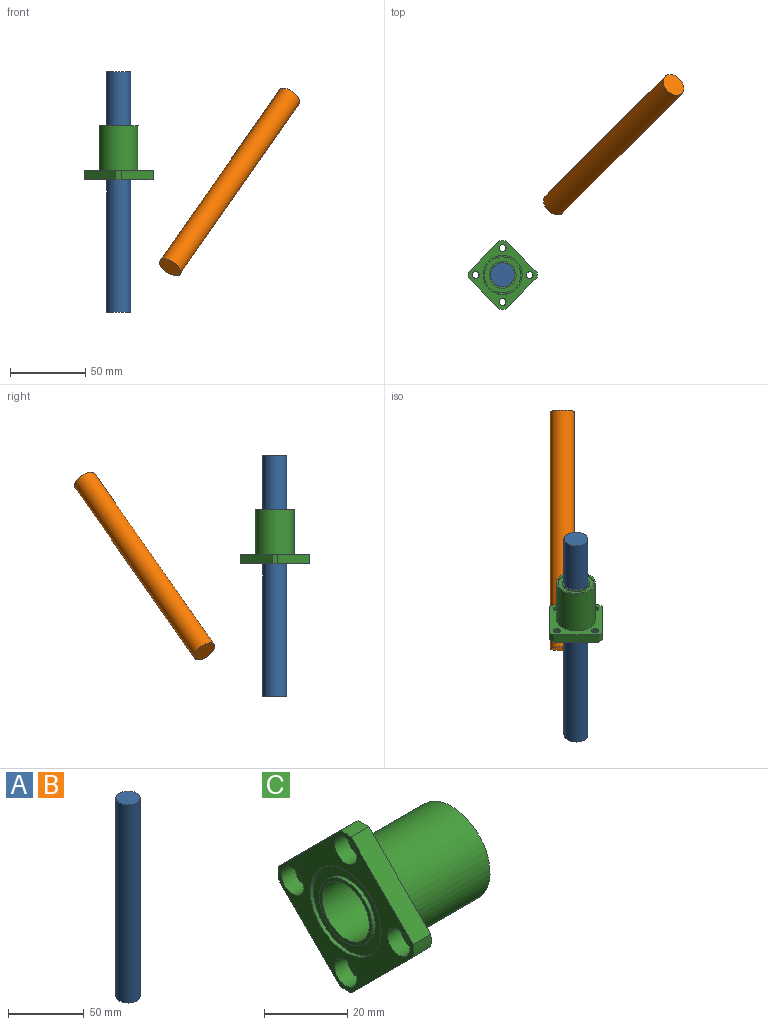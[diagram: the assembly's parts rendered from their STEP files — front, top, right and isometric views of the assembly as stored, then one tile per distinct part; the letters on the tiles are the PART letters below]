
ASSEMBLY  parts=3 mates=1
PART A: 3 faces, bbox 16x16x160 mm
  f0: cylinder r=8mm len=160mm, axis (0,0,1), area 8042.5mm2, adj f1,f2
  f1: plane 16x16mm, normal (0,0,1), area 201.1mm2, adj f0
  f2: plane 16x16mm, normal (0,0,-1), area 201.1mm2, adj f0
PART B: same geometry as A
PART C: 33 faces, bbox 36x46x46 mm
  f0: cylinder r=2.25mm len=4.5mm, axis (-1,0,0), area 22.6mm2, adj f17,f28
  f1: cylinder r=3.75mm len=7.5mm, axis (-1,0,0), area 103.7mm2, adj f18,f28
  f2: cylinder r=2.25mm len=4.5mm, axis (-1,0,0), area 22.6mm2, adj f17,f27
  f3: cylinder r=3.75mm len=7.5mm, axis (-1,0,0), area 103.7mm2, adj f18,f27
  f4: cylinder r=2.25mm len=4.5mm, axis (-1,0,0), area 22.6mm2, adj f17,f26
  f5: cylinder r=3.75mm len=7.5mm, axis (-1,0,0), area 103.7mm2, adj f18,f26
  f6: cylinder r=2.25mm len=4.5mm, axis (-1,0,0), area 22.6mm2, adj f17,f25
  f7: cylinder r=3.75mm len=7.5mm, axis (-1,0,0), area 103.7mm2, adj f18,f25
  f8: cylinder r=12mm len=24mm, axis (-1,0,0), area 75.4mm2, adj f18,f19
  f9: cylinder r=13mm len=30mm, axis (-1,0,0), area 2450.4mm2, adj f17,f23
  f10: cylinder r=12mm len=24mm, axis (-1,0,0), area 75.4mm2, adj f22,f23
  f11: cylinder r=9mm len=18mm, axis (-1,0,0), area 56.5mm2, adj f21,f22
  f12: cylinder r=8mm len=36mm, axis (-1,0,0), area 1809.6mm2, adj f20,f21
  f13: cylinder r=9mm len=18mm, axis (-1,0,0), area 56.5mm2, adj f19,f20
  f14: cylinder r=23mm len=6mm, axis (-1,0,0), area 21.9mm2, adj f17,f18,f30,f31
  f15: cylinder r=23mm len=6mm, axis (-1,0,0), area 21.9mm2, adj f17,f18,f31,f32
  f16: cylinder r=23mm len=6mm, axis (-1,0,0), area 21.9mm2, adj f17,f18,f29,f30
  f17: plane 46x46mm, normal (1,0,0), area 617.9mm2, adj f0,f2,f4,f6,f9,f14,f15,f16
  f18: plane 46x46mm, normal (-1,0,0), area 583.3mm2, adj f1,f3,f5,f7,f8,f14,f15,f16
  f19: plane 24x24mm, normal (-1,0,0), area 197.9mm2, adj f8,f13
  f20: plane 18x18mm, normal (-1,0,0), area 53.4mm2, adj f12,f13
  f21: plane 18x18mm, normal (1,0,0), area 53.4mm2, adj f11,f12
  f22: plane 24x24mm, normal (1,0,0), area 197.9mm2, adj f10,f11
  f23: plane 26x26mm, normal (1,0,0), area 78.5mm2, adj f9,f10
  f24: cylinder r=23mm len=6mm, axis (-1,0,0), area 21.9mm2, adj f17,f18,f29,f32
  f25: plane 7.5x7.5mm, normal (-1,0,0), area 28.3mm2, adj f6,f7
  f26: plane 7.5x7.5mm, normal (-1,0,0), area 28.3mm2, adj f4,f5
  f27: plane 7.5x7.5mm, normal (-1,0,0), area 28.3mm2, adj f2,f3
  f28: plane 7.5x7.5mm, normal (-1,0,0), area 28.3mm2, adj f0,f1
  f29: plane 21.11x21.11mm, normal (0,-0.71,-0.71), area 179.1mm2, adj f16,f17,f18,f24
  f30: plane 21.11x21.11mm, normal (0,-0.71,0.71), area 179.1mm2, adj f14,f16,f17,f18
  f31: plane 21.11x21.11mm, normal (0,0.71,0.71), area 179.1mm2, adj f14,f15,f17,f18
  f32: plane 21.11x21.11mm, normal (0,0.71,-0.71), area 179.1mm2, adj f15,f17,f18,f24
PLACE A t=(-99.7,-65.44,-11.83)mm fixed
PLACE B rot(axis=(-0.71,0.71,0),44.7deg) t=(-25.65,21.37,-5.18)mm
PLACE C rot(axis=(0,-1,0),90deg) t=(-99.7,-65.44,-3.63)mm
MATE slider C.f8 <-> A.f0  axis (0,0,-1) through (-99.7,-65.44,17.37)mm
